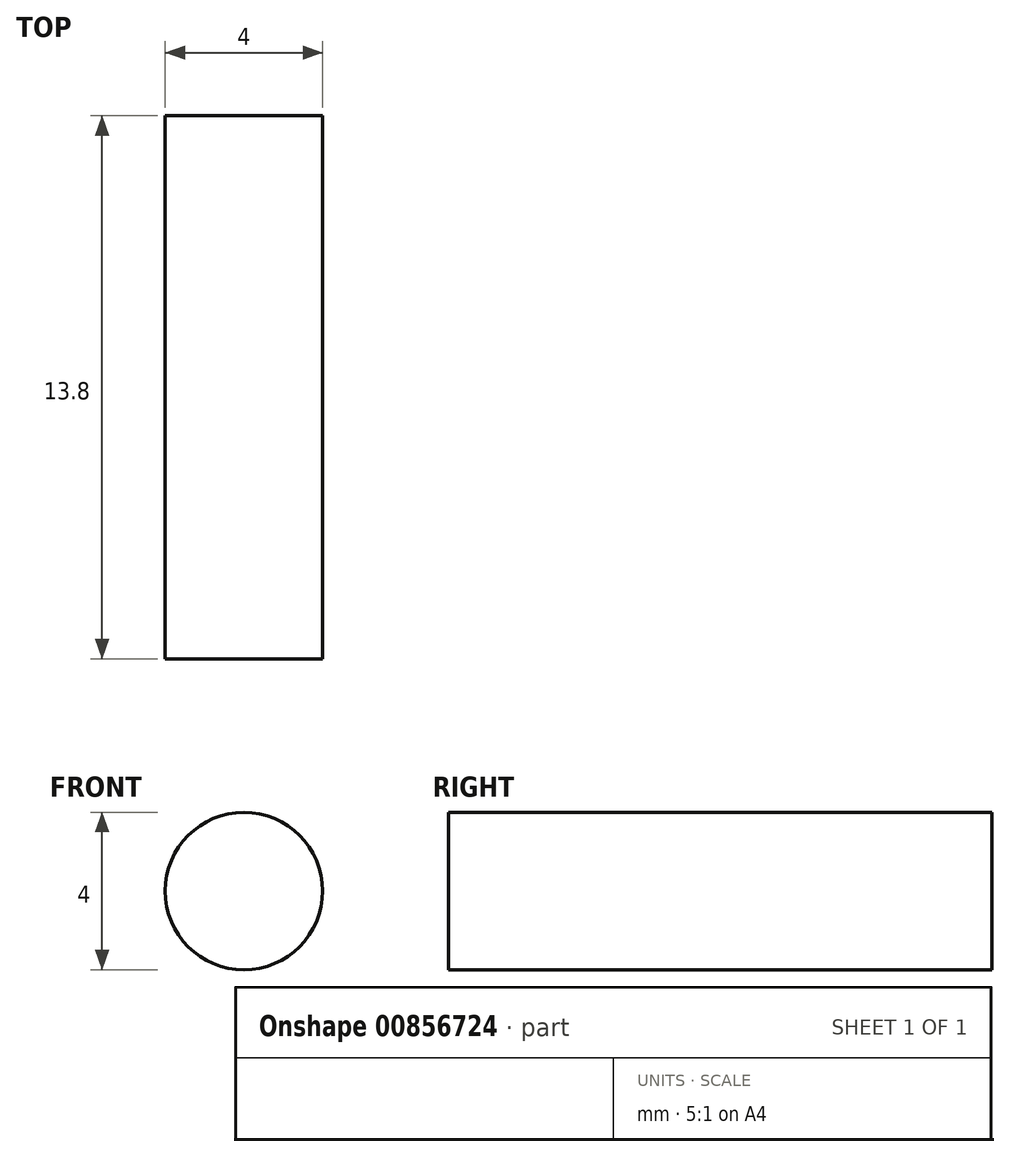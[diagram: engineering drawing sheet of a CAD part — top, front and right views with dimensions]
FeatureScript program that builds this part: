
annotation { "Feature Type Name" : "Feature", "Feature Type Description" : "" }
export const myFeature = defineFeature(function(context is Context, id is Id, definition is map)
    precondition{}
    {
        {
            var Q0;
            Q0=qCreatedBy(makeId("Front.planeOp"),FACE);
            var sketch = newSketch(context, id + "F0", { "sketchPlane" : qUnion([Q0])});
            skCircle(sketch, "E0", {"center": v(0, 0) * mm, "radius": 2 * mm});
            skSolve(sketch);
        }
        {
            var Q0;
            Q0 = qSketchRegion(id + "F0", true);
            extrude(context, id + "F1", {"entities" : qUnion([Q0]), "endBound" : BoundingType.SYMMETRIC, "depth" : 13.8 * mm, "offsetDistance" : 25 * mm});
        }
    });
